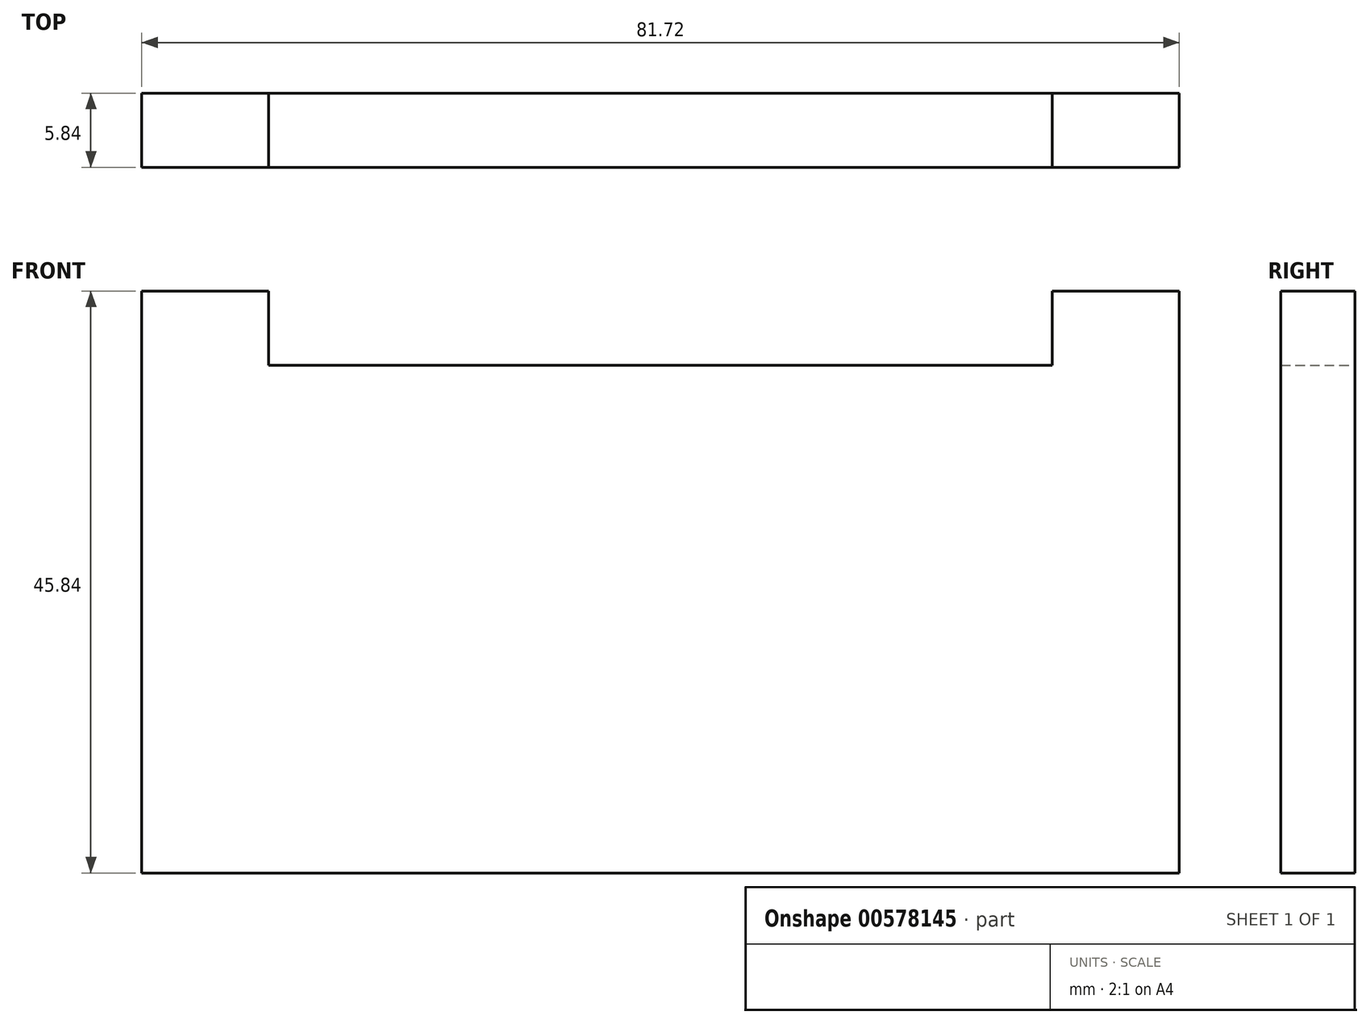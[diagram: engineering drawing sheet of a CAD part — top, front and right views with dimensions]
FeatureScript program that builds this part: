
annotation { "Feature Type Name" : "Feature", "Feature Type Description" : "" }
export const myFeature = defineFeature(function(context is Context, id is Id, definition is map)
    precondition{}
    {
        {
            var Q0;
            Q0=qCreatedBy(makeId("Front.planeOp"),FACE);
            var sketch = newSketch(context, id + "F0", { "sketchPlane" : qUnion([Q0])});
            skLineSegment(sketch, "E0.bottom", {"start": v(40.86, 22.92) * mm, "end": v(30.86, 22.92) * mm});
            skLineSegment(sketch, "E0.top", {"start": v(40.86, -22.92) * mm, "end": v(-40.86, -22.92) * mm});
            skLineSegment(sketch, "E0.left", {"start": v(40.86, 22.92) * mm, "end": v(40.86, -22.92) * mm});
            skLineSegment(sketch, "E0.right", {"start": v(-40.86, 22.92) * mm, "end": v(-40.86, -22.92) * mm});
            skPoint(sketch, "E0.middle", {"position": v(0, 0) * mm});
            skLineSegment(sketch, "E1.top", {"start": v(30.86, 17.08) * mm, "end": v(-30.86, 17.08) * mm});
            skLineSegment(sketch, "E1.left", {"start": v(30.86, 22.92) * mm, "end": v(30.86, 17.08) * mm});
            skLineSegment(sketch, "E1.right", {"start": v(-30.86, 22.92) * mm, "end": v(-30.86, 17.08) * mm});
            skPoint(sketch, "E1.middle", {"position": v(0, 20) * mm});
            skLineSegment(sketch, "E2.trimOffspring", {"start": v(-30.86, 22.92) * mm, "end": v(-40.86, 22.92) * mm});
            skSolve(sketch);
        }
        {
            var Q0;
            Q0=makeQuery(id+"F0.imprint","IMPRINT",FACE,{"disambiguationData":[TD([[makeQuery(id+"F0.imprint","IMPRINT",EDGE,{"derivedFrom":sQuery(id+"F0.wireOp",EDGE,"E0.bottom")}),1.0]])]});
            extrude(context, id + "F1", {"entities" : qUnion([Q0]), "depth" : 5.84 * mm, "offsetDistance" : 25 * mm});
        }
    });
